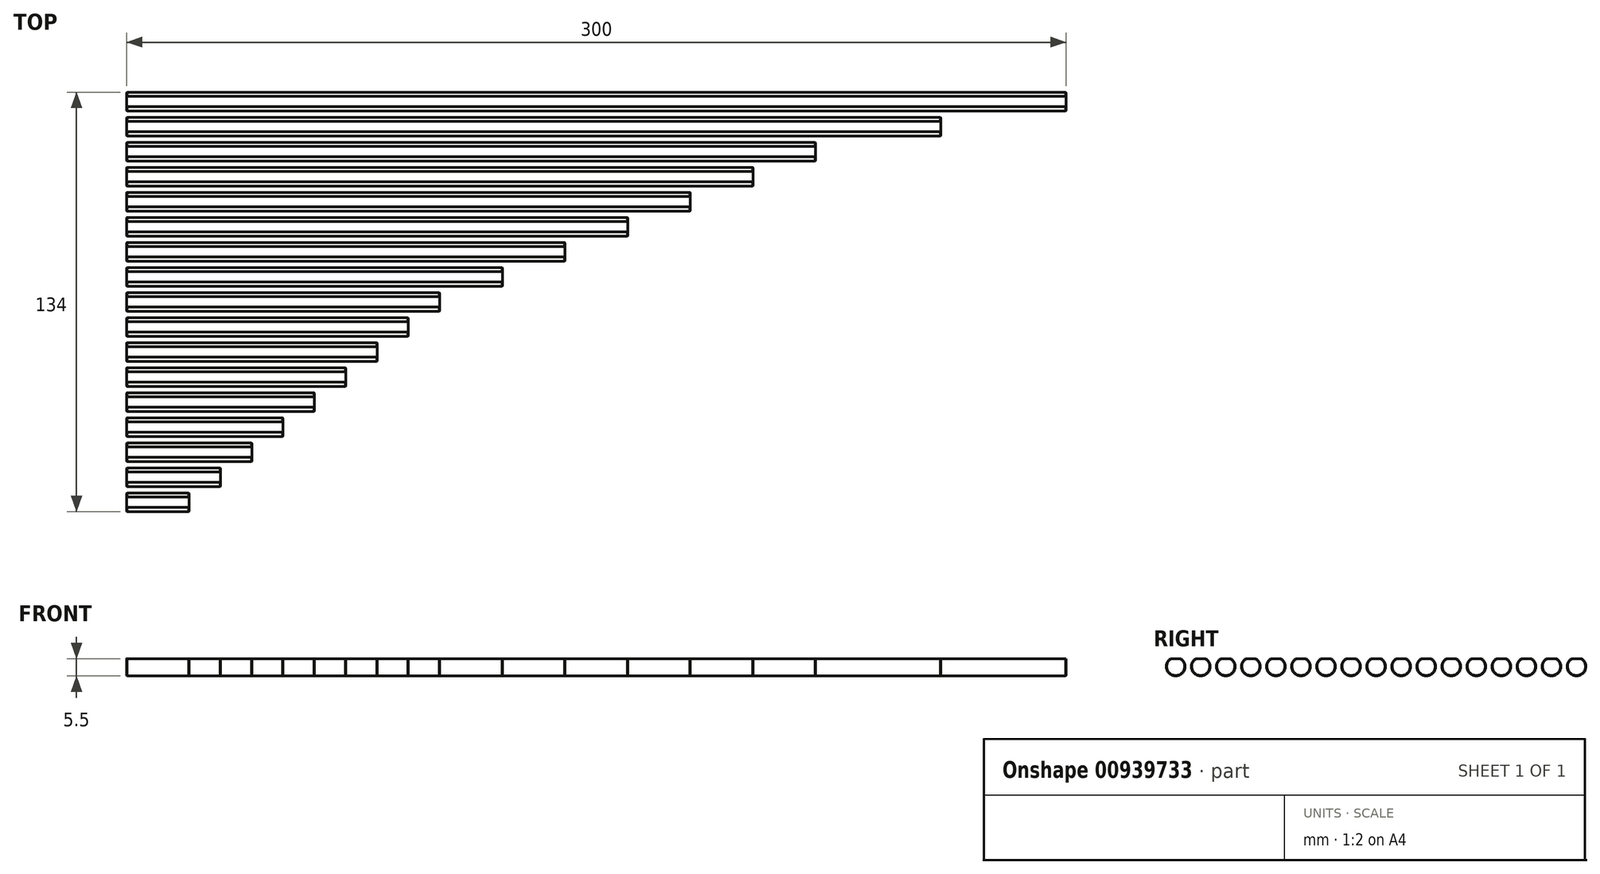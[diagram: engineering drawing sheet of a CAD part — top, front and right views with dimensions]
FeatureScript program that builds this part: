
annotation { "Feature Type Name" : "Feature", "Feature Type Description" : "" }
export const myFeature = defineFeature(function(context is Context, id is Id, definition is map)
    precondition{}
    {
        {
            var Q0;
            Q0=qCreatedBy(makeId("Right.planeOp"),FACE);
            var sketch = newSketch(context, id + "F0", { "sketchPlane" : qUnion([Q0])});
            skLineSegment(sketch, "E0", {"start": v(0, 3) * mm, "end": v(128, 3) * mm, "construction": true});
            skCircle(sketch, "E1", {"center": v(0, 0) * mm, "radius": 3 * mm});
            skCircle(sketch, "E2", {"center": v(8, 0) * mm, "radius": 3 * mm});
            skCircle(sketch, "E3", {"center": v(16, 0) * mm, "radius": 3 * mm});
            skCircle(sketch, "E4", {"center": v(24, 0) * mm, "radius": 3 * mm});
            skCircle(sketch, "E5", {"center": v(32, 0) * mm, "radius": 3 * mm});
            skCircle(sketch, "E6", {"center": v(40, 0) * mm, "radius": 3 * mm});
            skCircle(sketch, "E7", {"center": v(48, 0) * mm, "radius": 3 * mm});
            skCircle(sketch, "E8", {"center": v(56, 0) * mm, "radius": 3 * mm});
            skCircle(sketch, "E9", {"center": v(64, 0) * mm, "radius": 3 * mm});
            skCircle(sketch, "E10", {"center": v(72, 0) * mm, "radius": 3 * mm});
            skCircle(sketch, "E11", {"center": v(80, 0) * mm, "radius": 3 * mm});
            skLineSegment(sketch, "E12", {"start": v(0, 0) * mm, "end": v(8, 0) * mm, "construction": true});
            skLineSegment(sketch, "E13", {"start": v(16, 0) * mm, "end": v(24, 0) * mm, "construction": true});
            skLineSegment(sketch, "E14", {"start": v(32, 0) * mm, "end": v(40, 0) * mm, "construction": true});
            skLineSegment(sketch, "E15", {"start": v(48, 0) * mm, "end": v(40, 0) * mm, "construction": true});
            skLineSegment(sketch, "E16", {"start": v(24, 0) * mm, "end": v(32, 0) * mm, "construction": true});
            skLineSegment(sketch, "E17", {"start": v(8, 0) * mm, "end": v(16, 0) * mm, "construction": true});
            skLineSegment(sketch, "E18", {"start": v(48, 0) * mm, "end": v(56, 0) * mm, "construction": true});
            skLineSegment(sketch, "E19", {"start": v(56, 0) * mm, "end": v(64, 0) * mm, "construction": true});
            skLineSegment(sketch, "E20", {"start": v(64, 0) * mm, "end": v(72, 0) * mm, "construction": true});
            skLineSegment(sketch, "E21", {"start": v(72, 0) * mm, "end": v(80, 0) * mm, "construction": true});
            skLineSegment(sketch, "E22", {"start": v(80, 0) * mm, "end": v(88, 0) * mm, "construction": true});
            skLineSegment(sketch, "E23", {"start": v(88, 0) * mm, "end": v(96, 0) * mm, "construction": true});
            skLineSegment(sketch, "E24", {"start": v(96, 0) * mm, "end": v(104, 0) * mm, "construction": true});
            skLineSegment(sketch, "E25", {"start": v(104, 0) * mm, "end": v(112, 0) * mm, "construction": true});
            skLineSegment(sketch, "E26", {"start": v(112, 0) * mm, "end": v(120, 0) * mm, "construction": true});
            skCircle(sketch, "E27", {"center": v(88, 0) * mm, "radius": 3 * mm});
            skCircle(sketch, "E28", {"center": v(96, 0) * mm, "radius": 3 * mm});
            skCircle(sketch, "E29", {"center": v(104, 0) * mm, "radius": 3 * mm});
            skCircle(sketch, "E30", {"center": v(112, 0) * mm, "radius": 3 * mm});
            skCircle(sketch, "E31", {"center": v(120, 0) * mm, "radius": 3 * mm});
            skLineSegment(sketch, "E32", {"start": v(120, 0) * mm, "end": v(128, 0) * mm, "construction": true});
            skCircle(sketch, "E33", {"center": v(128, 0) * mm, "radius": 3 * mm});
            skLineSegment(sketch, "E34", {"start": v(-1.66, 2.5) * mm, "end": v(1.66, 2.5) * mm});
            skLineSegment(sketch, "E35.trimOffspring", {"start": v(6.34, 2.5) * mm, "end": v(9.66, 2.5) * mm});
            skLineSegment(sketch, "E36.trimOffspring", {"start": v(14.34, 2.5) * mm, "end": v(17.66, 2.5) * mm});
            skLineSegment(sketch, "E37.trimOffspring", {"start": v(22.34, 2.5) * mm, "end": v(25.66, 2.5) * mm});
            skLineSegment(sketch, "E38.trimOffspring", {"start": v(30.34, 2.5) * mm, "end": v(33.66, 2.5) * mm});
            skLineSegment(sketch, "E39.trimOffspring", {"start": v(38.34, 2.5) * mm, "end": v(41.66, 2.5) * mm});
            skLineSegment(sketch, "E40.trimOffspring", {"start": v(46.34, 2.5) * mm, "end": v(49.66, 2.5) * mm});
            skLineSegment(sketch, "E41.trimOffspring", {"start": v(54.34, 2.5) * mm, "end": v(57.66, 2.5) * mm});
            skLineSegment(sketch, "E42.trimOffspring", {"start": v(62.34, 2.5) * mm, "end": v(65.66, 2.5) * mm});
            skLineSegment(sketch, "E43.trimOffspring", {"start": v(78.34, 2.5) * mm, "end": v(81.66, 2.5) * mm});
            skLineSegment(sketch, "E44.trimOffspring", {"start": v(70.34, 2.5) * mm, "end": v(73.66, 2.5) * mm});
            skLineSegment(sketch, "E45.trimOffspring", {"start": v(86.34, 2.5) * mm, "end": v(89.66, 2.5) * mm});
            skLineSegment(sketch, "E46.trimOffspring", {"start": v(94.34, 2.5) * mm, "end": v(97.66, 2.5) * mm});
            skLineSegment(sketch, "E47.trimOffspring", {"start": v(102.34, 2.5) * mm, "end": v(105.66, 2.5) * mm});
            skLineSegment(sketch, "E48.trimOffspring", {"start": v(110.34, 2.5) * mm, "end": v(113.66, 2.5) * mm});
            skLineSegment(sketch, "E49.trimOffspring", {"start": v(118.34, 2.5) * mm, "end": v(121.66, 2.5) * mm});
            skLineSegment(sketch, "E50.trimOffspring", {"start": v(126.34, 2.5) * mm, "end": v(129.66, 2.5) * mm});
            skSolve(sketch);
        }
        {
            var Q0;
            {var subQ0=sQuery(id+"F0.wireOp",EDGE,"E34");Q0=makeQuery(id+"F0.imprint","IMPRINT",FACE,{"disambiguationData":[TD([[makeQuery(id+"F0.imprint","IMPRINT",EDGE,{"derivedFrom":subQ0}),-1.0]])]});}
            extrude(context, id + "F1", {"entities" : qUnion([Q0]), "depth" : 20 * mm, "offsetDistance" : 25 * mm});
        }
        {
            var Q0;
            {var subQ0=sQuery(id+"F0.wireOp",EDGE,"E35.trimOffspring");Q0=makeQuery(id+"F0.imprint","IMPRINT",FACE,{"disambiguationData":[TD([[makeQuery(id+"F0.imprint","IMPRINT",EDGE,{"derivedFrom":subQ0}),-1.0]])]});}
            extrude(context, id + "F2", {"entities" : qUnion([Q0]), "depth" : 30 * mm, "offsetDistance" : 25 * mm});
        }
        {
            var Q0;
            {var subQ0=sQuery(id+"F0.wireOp",EDGE,"E36.trimOffspring");Q0=makeQuery(id+"F0.imprint","IMPRINT",FACE,{"disambiguationData":[TD([[makeQuery(id+"F0.imprint","IMPRINT",EDGE,{"derivedFrom":subQ0}),-1.0]])]});}
            extrude(context, id + "F3", {"entities" : qUnion([Q0]), "depth" : 40 * mm, "offsetDistance" : 25 * mm});
        }
        {
            var Q0;
            {var subQ0=sQuery(id+"F0.wireOp",EDGE,"E37.trimOffspring");Q0=makeQuery(id+"F0.imprint","IMPRINT",FACE,{"disambiguationData":[TD([[makeQuery(id+"F0.imprint","IMPRINT",EDGE,{"derivedFrom":subQ0}),-1.0]])]});}
            extrude(context, id + "F4", {"entities" : qUnion([Q0]), "depth" : 50 * mm, "offsetDistance" : 25 * mm});
        }
        {
            var Q0;
            {var subQ0=sQuery(id+"F0.wireOp",EDGE,"E38.trimOffspring");Q0=makeQuery(id+"F0.imprint","IMPRINT",FACE,{"disambiguationData":[TD([[makeQuery(id+"F0.imprint","IMPRINT",EDGE,{"derivedFrom":subQ0}),-1.0]])]});}
            extrude(context, id + "F5", {"entities" : qUnion([Q0]), "depth" : 60 * mm, "offsetDistance" : 25 * mm});
        }
        {
            var Q0;
            {var subQ0=sQuery(id+"F0.wireOp",EDGE,"E39.trimOffspring");Q0=makeQuery(id+"F0.imprint","IMPRINT",FACE,{"disambiguationData":[TD([[makeQuery(id+"F0.imprint","IMPRINT",EDGE,{"derivedFrom":subQ0}),-1.0]])]});}
            extrude(context, id + "F6", {"entities" : qUnion([Q0]), "depth" : 70 * mm, "offsetDistance" : 25 * mm});
        }
        {
            var Q0;
            {var subQ0=sQuery(id+"F0.wireOp",EDGE,"E40.trimOffspring");Q0=makeQuery(id+"F0.imprint","IMPRINT",FACE,{"disambiguationData":[TD([[makeQuery(id+"F0.imprint","IMPRINT",EDGE,{"derivedFrom":subQ0}),-1.0]])]});}
            extrude(context, id + "F7", {"entities" : qUnion([Q0]), "depth" : 80 * mm, "offsetDistance" : 25 * mm});
        }
        {
            var Q0;
            {var subQ0=sQuery(id+"F0.wireOp",EDGE,"E41.trimOffspring");Q0=makeQuery(id+"F0.imprint","IMPRINT",FACE,{"disambiguationData":[TD([[makeQuery(id+"F0.imprint","IMPRINT",EDGE,{"derivedFrom":subQ0}),-1.0]])]});}
            extrude(context, id + "F8", {"entities" : qUnion([Q0]), "depth" : 90 * mm, "offsetDistance" : 25 * mm});
        }
        {
            var Q0;
            {var subQ0=sQuery(id+"F0.wireOp",EDGE,"E42.trimOffspring");Q0=makeQuery(id+"F0.imprint","IMPRINT",FACE,{"disambiguationData":[TD([[makeQuery(id+"F0.imprint","IMPRINT",EDGE,{"derivedFrom":subQ0}),-1.0]])]});}
            extrude(context, id + "F9", {"entities" : qUnion([Q0]), "depth" : 100 * mm, "offsetDistance" : 25 * mm});
        }
        {
            var Q0;
            {var subQ0=sQuery(id+"F0.wireOp",EDGE,"E44.trimOffspring");Q0=makeQuery(id+"F0.imprint","IMPRINT",FACE,{"disambiguationData":[TD([[makeQuery(id+"F0.imprint","IMPRINT",EDGE,{"derivedFrom":subQ0}),-1.0]])]});}
            extrude(context, id + "F10", {"entities" : qUnion([Q0]), "depth" : 120 * mm, "offsetDistance" : 25 * mm});
        }
        {
            var Q0;
            {var subQ0=sQuery(id+"F0.wireOp",EDGE,"E43.trimOffspring");Q0=makeQuery(id+"F0.imprint","IMPRINT",FACE,{"disambiguationData":[TD([[makeQuery(id+"F0.imprint","IMPRINT",EDGE,{"derivedFrom":subQ0}),-1.0]])]});}
            extrude(context, id + "F11", {"entities" : qUnion([Q0]), "depth" : 140 * mm, "offsetDistance" : 25 * mm});
        }
        {
            var Q0;
            {var subQ0=sQuery(id+"F0.wireOp",EDGE,"E45.trimOffspring");Q0=makeQuery(id+"F0.imprint","IMPRINT",FACE,{"disambiguationData":[TD([[makeQuery(id+"F0.imprint","IMPRINT",EDGE,{"derivedFrom":subQ0}),-1.0]])]});}
            extrude(context, id + "F12", {"entities" : qUnion([Q0]), "depth" : 160 * mm, "offsetDistance" : 25 * mm});
        }
        {
            var Q0;
            {var subQ0=sQuery(id+"F0.wireOp",EDGE,"E46.trimOffspring");Q0=makeQuery(id+"F0.imprint","IMPRINT",FACE,{"disambiguationData":[TD([[makeQuery(id+"F0.imprint","IMPRINT",EDGE,{"derivedFrom":subQ0}),-1.0]])]});}
            extrude(context, id + "F13", {"entities" : qUnion([Q0]), "depth" : 180 * mm, "offsetDistance" : 25 * mm});
        }
        {
            var Q0;
            {var subQ0=sQuery(id+"F0.wireOp",EDGE,"E47.trimOffspring");Q0=makeQuery(id+"F0.imprint","IMPRINT",FACE,{"disambiguationData":[TD([[makeQuery(id+"F0.imprint","IMPRINT",EDGE,{"derivedFrom":subQ0}),-1.0]])]});}
            extrude(context, id + "F14", {"entities" : qUnion([Q0]), "depth" : 200 * mm, "offsetDistance" : 25 * mm});
        }
        {
            var Q0;
            {var subQ0=sQuery(id+"F0.wireOp",EDGE,"E48.trimOffspring");Q0=makeQuery(id+"F0.imprint","IMPRINT",FACE,{"disambiguationData":[TD([[makeQuery(id+"F0.imprint","IMPRINT",EDGE,{"derivedFrom":subQ0}),-1.0]])]});}
            extrude(context, id + "F15", {"entities" : qUnion([Q0]), "depth" : 220 * mm, "offsetDistance" : 25 * mm});
        }
        {
            var Q0;
            {var subQ0=sQuery(id+"F0.wireOp",EDGE,"E49.trimOffspring");Q0=makeQuery(id+"F0.imprint","IMPRINT",FACE,{"disambiguationData":[TD([[makeQuery(id+"F0.imprint","IMPRINT",EDGE,{"derivedFrom":subQ0}),-1.0]])]});}
            extrude(context, id + "F16", {"entities" : qUnion([Q0]), "depth" : 260 * mm, "offsetDistance" : 25 * mm});
        }
        {
            var Q0;
            {var subQ0=sQuery(id+"F0.wireOp",EDGE,"E50.trimOffspring");Q0=makeQuery(id+"F0.imprint","IMPRINT",FACE,{"disambiguationData":[TD([[makeQuery(id+"F0.imprint","IMPRINT",EDGE,{"derivedFrom":subQ0}),-1.0]])]});}
            extrude(context, id + "F17", {"entities" : qUnion([Q0]), "depth" : 300 * mm, "offsetDistance" : 25 * mm});
        }
        {
            var Q0;
            Q0=makeQuery(id+"F17.opExtrude","CAP_EDGE",EDGE,{"disambiguationData":[OSD([sQuery(id+"F0.wireOp",EDGE,"E33")])],"isStart":true});
            var Q1;
            Q1=makeQuery(id+"F16.opExtrude","CAP_EDGE",EDGE,{"disambiguationData":[OSD([sQuery(id+"F0.wireOp",EDGE,"E31")])],"isStart":true});
            var Q2;
            Q2=makeQuery(id+"F15.opExtrude","CAP_EDGE",EDGE,{"disambiguationData":[OSD([sQuery(id+"F0.wireOp",EDGE,"E30")])],"isStart":true});
            var Q3;
            Q3=makeQuery(id+"F14.opExtrude","CAP_EDGE",EDGE,{"disambiguationData":[OSD([sQuery(id+"F0.wireOp",EDGE,"E29")])],"isStart":true});
            var Q4;
            Q4=makeQuery(id+"F13.opExtrude","CAP_EDGE",EDGE,{"disambiguationData":[OSD([sQuery(id+"F0.wireOp",EDGE,"E28")])],"isStart":true});
            var Q5;
            Q5=makeQuery(id+"F12.opExtrude","CAP_EDGE",EDGE,{"disambiguationData":[OSD([sQuery(id+"F0.wireOp",EDGE,"E27")])],"isStart":true});
            var Q6;
            Q6=makeQuery(id+"F11.opExtrude","CAP_EDGE",EDGE,{"disambiguationData":[OSD([sQuery(id+"F0.wireOp",EDGE,"E11")])],"isStart":true});
            var Q7;
            Q7=makeQuery(id+"F10.opExtrude","CAP_EDGE",EDGE,{"disambiguationData":[OSD([sQuery(id+"F0.wireOp",EDGE,"E10")])],"isStart":true});
            var Q8;
            Q8=makeQuery(id+"F9.opExtrude","CAP_EDGE",EDGE,{"disambiguationData":[OSD([sQuery(id+"F0.wireOp",EDGE,"E9")])],"isStart":true});
            var Q9;
            Q9=makeQuery(id+"F8.opExtrude","CAP_EDGE",EDGE,{"disambiguationData":[OSD([sQuery(id+"F0.wireOp",EDGE,"E8")])],"isStart":true});
            var Q10;
            Q10=makeQuery(id+"F7.opExtrude","CAP_EDGE",EDGE,{"disambiguationData":[OSD([sQuery(id+"F0.wireOp",EDGE,"E7")])],"isStart":true});
            var Q11;
            Q11=makeQuery(id+"F6.opExtrude","CAP_EDGE",EDGE,{"disambiguationData":[OSD([sQuery(id+"F0.wireOp",EDGE,"E6")])],"isStart":true});
            var Q12;
            Q12=makeQuery(id+"F5.opExtrude","CAP_EDGE",EDGE,{"disambiguationData":[OSD([sQuery(id+"F0.wireOp",EDGE,"E5")])],"isStart":true});
            var Q13;
            Q13=makeQuery(id+"F4.opExtrude","CAP_EDGE",EDGE,{"disambiguationData":[OSD([sQuery(id+"F0.wireOp",EDGE,"E4")])],"isStart":true});
            var Q14;
            Q14=makeQuery(id+"F3.opExtrude","CAP_EDGE",EDGE,{"disambiguationData":[OSD([sQuery(id+"F0.wireOp",EDGE,"E3")])],"isStart":true});
            var Q15;
            Q15=makeQuery(id+"F2.opExtrude","CAP_EDGE",EDGE,{"disambiguationData":[OSD([sQuery(id+"F0.wireOp",EDGE,"E2")])],"isStart":true});
            var Q16;
            Q16=makeQuery(id+"F1.opExtrude","CAP_EDGE",EDGE,{"disambiguationData":[OSD([sQuery(id+"F0.wireOp",EDGE,"E1")])],"isStart":true});
            var Q17;
            Q17=makeQuery(id+"F1.opExtrude","CAP_EDGE",EDGE,{"disambiguationData":[OSD([sQuery(id+"F0.wireOp",EDGE,"E1")])],"isStart":false});
            var Q18;
            Q18=makeQuery(id+"F2.opExtrude","CAP_EDGE",EDGE,{"disambiguationData":[OSD([sQuery(id+"F0.wireOp",EDGE,"E2")])],"isStart":false});
            var Q19;
            Q19=makeQuery(id+"F3.opExtrude","CAP_EDGE",EDGE,{"disambiguationData":[OSD([sQuery(id+"F0.wireOp",EDGE,"E3")])],"isStart":false});
            var Q20;
            Q20=makeQuery(id+"F4.opExtrude","CAP_EDGE",EDGE,{"disambiguationData":[OSD([sQuery(id+"F0.wireOp",EDGE,"E4")])],"isStart":false});
            var Q21;
            Q21=makeQuery(id+"F5.opExtrude","CAP_EDGE",EDGE,{"disambiguationData":[OSD([sQuery(id+"F0.wireOp",EDGE,"E5")])],"isStart":false});
            var Q22;
            Q22=makeQuery(id+"F6.opExtrude","CAP_EDGE",EDGE,{"disambiguationData":[OSD([sQuery(id+"F0.wireOp",EDGE,"E6")])],"isStart":false});
            var Q23;
            Q23=makeQuery(id+"F7.opExtrude","CAP_EDGE",EDGE,{"disambiguationData":[OSD([sQuery(id+"F0.wireOp",EDGE,"E7")])],"isStart":false});
            var Q24;
            Q24=makeQuery(id+"F8.opExtrude","CAP_EDGE",EDGE,{"disambiguationData":[OSD([sQuery(id+"F0.wireOp",EDGE,"E8")])],"isStart":false});
            var Q25;
            Q25=makeQuery(id+"F9.opExtrude","CAP_EDGE",EDGE,{"disambiguationData":[OSD([sQuery(id+"F0.wireOp",EDGE,"E9")])],"isStart":false});
            var Q26;
            Q26=makeQuery(id+"F17.opExtrude","CAP_EDGE",EDGE,{"disambiguationData":[OSD([sQuery(id+"F0.wireOp",EDGE,"E33")])],"isStart":false});
            var Q27;
            Q27=makeQuery(id+"F16.opExtrude","CAP_EDGE",EDGE,{"disambiguationData":[OSD([sQuery(id+"F0.wireOp",EDGE,"E31")])],"isStart":false});
            var Q28;
            Q28=makeQuery(id+"F15.opExtrude","CAP_EDGE",EDGE,{"disambiguationData":[OSD([sQuery(id+"F0.wireOp",EDGE,"E30")])],"isStart":false});
            var Q29;
            Q29=makeQuery(id+"F14.opExtrude","CAP_EDGE",EDGE,{"disambiguationData":[OSD([sQuery(id+"F0.wireOp",EDGE,"E29")])],"isStart":false});
            var Q30;
            Q30=makeQuery(id+"F13.opExtrude","CAP_EDGE",EDGE,{"disambiguationData":[OSD([sQuery(id+"F0.wireOp",EDGE,"E28")])],"isStart":false});
            var Q31;
            Q31=makeQuery(id+"F12.opExtrude","CAP_EDGE",EDGE,{"disambiguationData":[OSD([sQuery(id+"F0.wireOp",EDGE,"E27")])],"isStart":false});
            var Q32;
            Q32=makeQuery(id+"F11.opExtrude","CAP_EDGE",EDGE,{"disambiguationData":[OSD([sQuery(id+"F0.wireOp",EDGE,"E11")])],"isStart":false});
            var Q33;
            Q33=makeQuery(id+"F10.opExtrude","CAP_EDGE",EDGE,{"disambiguationData":[OSD([sQuery(id+"F0.wireOp",EDGE,"E10")])],"isStart":false});
            chamfer(context, id + "F18", {"entities" : qUnion([Q0, Q1, Q2, Q3, Q4, Q5, Q6, Q7, Q8, Q9, Q10, Q11, Q12, Q13, Q14, Q15, Q16, Q17, Q18, Q19, Q20, Q21, Q22, Q23, Q24, Q25, Q26, Q27, Q28, Q29, Q30, Q31, Q32, Q33]), "width" : 0.12 * mm, "tangentPropagation" : true});
        }
    });
